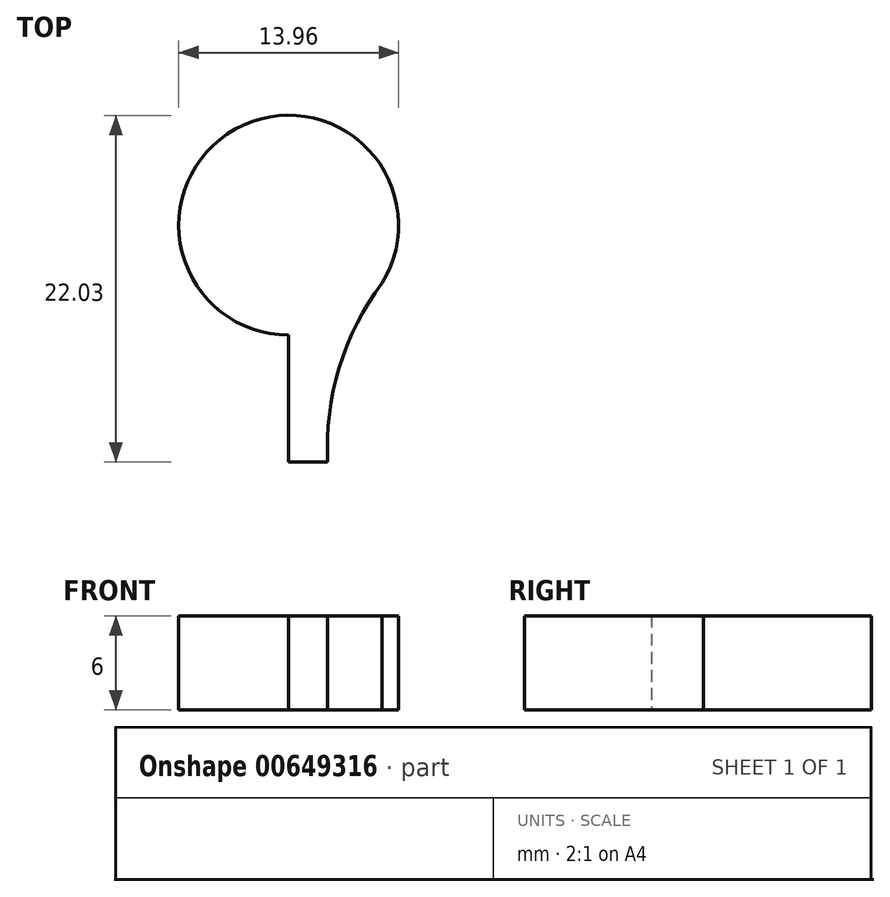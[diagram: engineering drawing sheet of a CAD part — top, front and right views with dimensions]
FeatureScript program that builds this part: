
annotation { "Feature Type Name" : "Feature", "Feature Type Description" : "" }
export const myFeature = defineFeature(function(context is Context, id is Id, definition is map)
    precondition{}
    {
        {
            var Q0;
            Q0=qCreatedBy(makeId("Top.planeOp"),FACE);
            var sketch = newSketch(context, id + "F0", { "sketchPlane" : qUnion([Q0])});
            skLineSegment(sketch, "E0", {"start": v(-0.81, -7) * mm, "end": v(-0.81, -15.07) * mm});
            skLineSegment(sketch, "E1", {"start": v(-0.81, -15.07) * mm, "end": v(1.68, -15.07) * mm});
            skArc(sketch, "E2", {"start": v(5.13, -3.7) * mm, "mid": v(2.4, -9.08) * mm, "end": v(1.68, -15.07) * mm});
            skArc(sketch, "E3", {"start": v(5.13, -3.7) * mm, "mid": v(-4.2, 6.08) * mm, "end": v(-0.81, -7) * mm});
            skSolve(sketch);
        }
        {
            var Q0;
            Q0=makeQuery(id+"F0.imprint","IMPRINT",FACE,{"disambiguationData":[TD([[makeQuery(id+"F0.imprint","IMPRINT",EDGE,{"derivedFrom":sQuery(id+"F0.wireOp",EDGE,"E0")}),1.0]])]});
            extrude(context, id + "F1", {"entities" : qUnion([Q0]), "depth" : 6 * mm, "offsetDistance" : 25 * mm});
        }
    });
